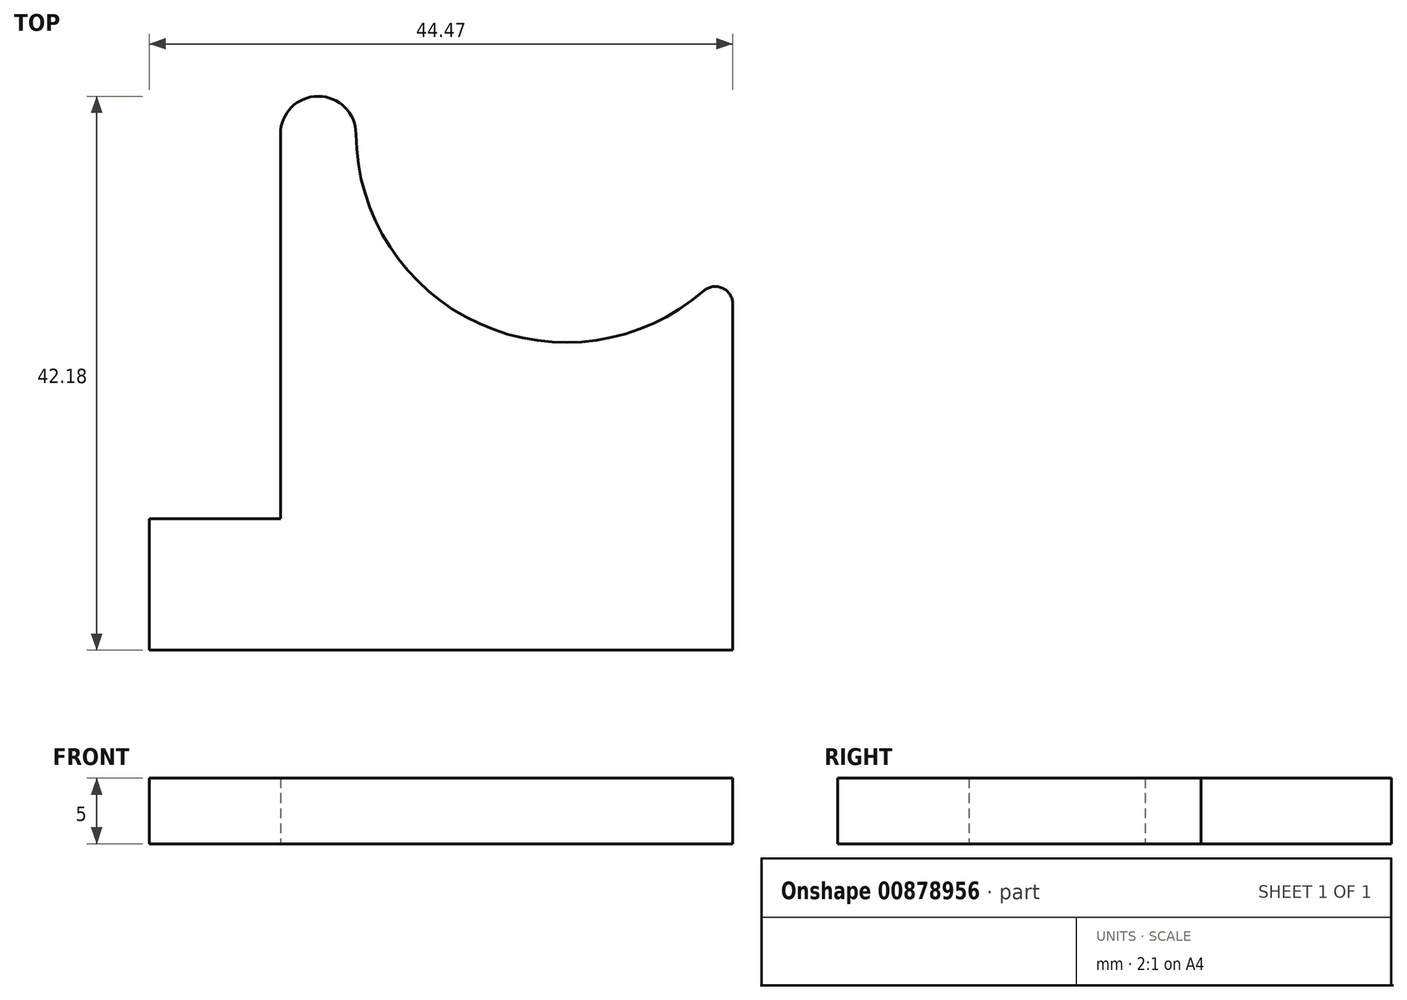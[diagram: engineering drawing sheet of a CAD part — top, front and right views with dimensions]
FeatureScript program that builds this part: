
annotation { "Feature Type Name" : "Feature", "Feature Type Description" : "" }
export const myFeature = defineFeature(function(context is Context, id is Id, definition is map)
    precondition{}
    {
        {
            var Q0;
            Q0=qCreatedBy(makeId("Top.planeOp"),FACE);
            var sketch = newSketch(context, id + "F0", { "sketchPlane" : qUnion([Q0])});
            skLineSegment(sketch, "E0.bottom", {"start": v(0, 0) * mm, "end": v(34.47, 0) * mm});
            skLineSegment(sketch, "E0.left", {"start": v(0, 0) * mm, "end": v(0, 29.3) * mm});
            skLineSegment(sketch, "E0.right", {"start": v(34.47, 0) * mm, "end": v(34.47, 16.35) * mm});
            skArc(sketch, "E1", {"start": v(5.76, 29.32) * mm, "mid": v(15.17, 14.85) * mm, "end": v(32.26, 17.36) * mm});
            skCircle(sketch, "E2", {"center": v(33.13, 16.35) * mm, "radius": 1.34 * mm});
            skCircle(sketch, "E3", {"center": v(2.88, 29.3) * mm, "radius": 2.88 * mm});
            skSolve(sketch);
        }
        {
            var Q0;
            Q0 = qSketchRegion(id + "F0", true);
            extrude(context, id + "F1", {"entities" : qUnion([Q0]), "depth" : 5 * mm, "offsetDistance" : 25 * mm});
        }
        {
            var Q0;
            Q0=makeQuery(id+"F1.opExtrude","CAP_FACE",FACE,{"disambiguationData":[OSD([sQuery(id+"F0.wireOp",EDGE,"E0.bottom"),sQuery(id+"F0.wireOp",EDGE,"E0.left"),sQuery(id+"F0.wireOp",EDGE,"E0.right"),sQuery(id+"F0.wireOp",EDGE,"E1"),sQuery(id+"F0.wireOp",EDGE,"E2"),sQuery(id+"F0.wireOp",EDGE,"E3")])],"isStart":false});
            var sketch = newSketch(context, id + "F2", { "sketchPlane" : qUnion([Q0])});
            skLineSegment(sketch, "E4", {"start": v(34.47, 0) * mm, "end": v(34.47, -10) * mm});
            skLineSegment(sketch, "E5", {"start": v(34.47, -10) * mm, "end": v(0, -10) * mm});
            skLineSegment(sketch, "E6", {"start": v(0, -10) * mm, "end": v(0, 0) * mm});
            skLineSegment(sketch, "E7", {"start": v(0, 0) * mm, "end": v(-10, 0) * mm});
            skLineSegment(sketch, "E8", {"start": v(0, 25.49) * mm, "end": v(-110.38, 52.94) * mm});
            skLineSegment(sketch, "E9", {"start": v(0, -10) * mm, "end": v(-10, -10) * mm});
            skLineSegment(sketch, "E10", {"start": v(-10, -10) * mm, "end": v(-10, 0) * mm});
            skSolve(sketch);
        }
        {
            var Q0;
            {var subQ0=makeQuery(id+"F1.opExtrude","CAP_EDGE",EDGE,{"disambiguationData":[OSD([sQuery(id+"F0.wireOp",EDGE,"E0.bottom")])],"isStart":false});Q0=makeQuery(id+"F2.imprint","IMPRINT",FACE,{"disambiguationData":[TD([[makeQuery(id+"F2.imprint","IMPRINT",EDGE,{"derivedFrom":subQ0}),1.0]])]});}
            var Q1;
            Q1=makeQuery(id+"F2.imprint","IMPRINT",FACE,{"disambiguationData":[TD([[makeQuery(id+"F2.imprint","IMPRINT",EDGE,{"derivedFrom":sQuery(id+"F2.wireOp",EDGE,"E4")}),-1.0]])]});
            var Q2;
            {var subQ0=sQuery(id+"F2.wireOp",EDGE,"E7");Q2=makeQuery(id+"F2.imprint","IMPRINT",FACE,{"disambiguationData":[TD([[makeQuery(id+"F2.imprint","IMPRINT",EDGE,{"derivedFrom":subQ0}),-1.0]])]});}
            var Q3;
            Q3=makeQuery(id+"F2.imprint","IMPRINT",FACE,{"disambiguationData":[TD([[makeQuery(id+"F2.imprint","IMPRINT",EDGE,{"derivedFrom":sQuery(id+"F2.wireOp",EDGE,"E6")}),1.0]])]});
            extrude(context, id + "F3", {"entities" : qUnion([Q0, Q1, Q2, Q3]), "operationType" : NewBodyOperationType.ADD, "oppositeDirection" : true, "depth" : 5 * mm, "offsetDistance" : 25 * mm});
        }
    });
